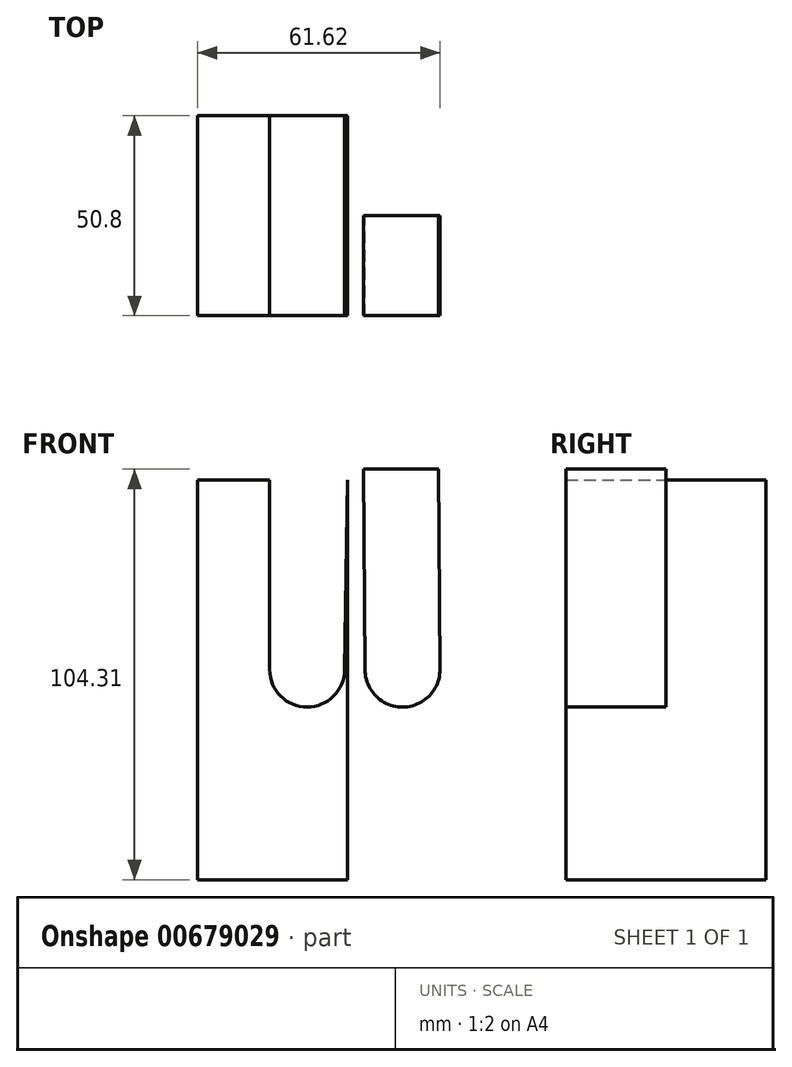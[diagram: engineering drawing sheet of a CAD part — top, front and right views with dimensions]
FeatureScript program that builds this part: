
annotation { "Feature Type Name" : "Feature", "Feature Type Description" : "" }
export const myFeature = defineFeature(function(context is Context, id is Id, definition is map)
    precondition{}
    {
        {
            var Q0;
            Q0=qCreatedBy(makeId("Front.planeOp"),FACE);
            var sketch = newSketch(context, id + "F0", { "sketchPlane" : qUnion([Q0])});
            skCircle(sketch, "E0", {"center": v(0, 0) * mm, "radius": 9.53 * mm});
            skLineSegment(sketch, "E1", {"start": v(-9.91, 50.92) * mm, "end": v(9.14, 50.92) * mm});
            skLineSegment(sketch, "E2", {"start": v(-9.52, 0) * mm, "end": v(-9.91, 50.92) * mm});
            skLineSegment(sketch, "E3", {"start": v(9.53, 0) * mm, "end": v(9.14, 50.92) * mm});
            skSolve(sketch);
        }
        {
            var Q0;
            Q0 = qSketchRegion(id + "F0", true);
            extrude(context, id + "F1", {"entities" : qUnion([Q0]), "depth" : 25.4 * mm, "offsetDistance" : 25.4 * mm});
        }
        {
            var Q0;
            Q0=qCreatedBy(makeId("Front.planeOp"),FACE);
            var sketch = newSketch(context, id + "F2", { "sketchPlane" : qUnion([Q0])});
            skLineSegment(sketch, "E4.bottom", {"start": v(-52.09, 48.2) * mm, "end": v(-13.99, 48.2) * mm});
            skLineSegment(sketch, "E4.top", {"start": v(-52.09, -53.4) * mm, "end": v(-13.99, -53.4) * mm});
            skLineSegment(sketch, "E4.left", {"start": v(-52.09, 48.2) * mm, "end": v(-52.09, -53.4) * mm});
            skLineSegment(sketch, "E4.right", {"start": v(-13.99, 48.2) * mm, "end": v(-13.99, -53.4) * mm});
            skCircle(sketch, "E5", {"center": v(-24.24, 0) * mm, "radius": 9.53 * mm});
            skLineSegment(sketch, "E6", {"start": v(-33.76, 0) * mm, "end": v(-33.76, 48.2) * mm});
            skLineSegment(sketch, "E7", {"start": v(-33.76, 0) * mm, "end": v(-14.71, 0) * mm});
            skLineSegment(sketch, "E8", {"start": v(-14.71, 0) * mm, "end": v(-13.99, 48.2) * mm});
            skSolve(sketch);
        }
        {
            var Q0;
            {var subQ2=sQuery(id+"F2.wireOp",EDGE,"E6");Q0=makeQuery(id+"F2.imprint","IMPRINT",FACE,{"disambiguationData":[TD([[makeQuery(id+"F2.imprint","IMPRINT",EDGE,{"derivedFrom":subQ2}),-1.0]])]});}
            var Q1;
            {var subQ0=sQuery(id+"F2.wireOp",EDGE,"E7");Q1=makeQuery(id+"F2.imprint","IMPRINT",FACE,{"disambiguationData":[TD([[makeQuery(id+"F2.imprint","IMPRINT",EDGE,{"derivedFrom":subQ0}),1.0]])]});}
            var Q2;
            {var subQ0=sQuery(id+"F2.wireOp",EDGE,"E7");Q2=makeQuery(id+"F2.imprint","IMPRINT",FACE,{"disambiguationData":[TD([[makeQuery(id+"F2.imprint","IMPRINT",EDGE,{"derivedFrom":subQ0}),-1.0]])]});}
            extrude(context, id + "F3", {"entities" : qUnion([Q0, Q1, Q2]), "operationType" : NewBodyOperationType.REMOVE, "oppositeDirection" : true, "depth" : 25.4 * mm, "offsetDistance" : 25.4 * mm});
        }
        {
            var Q0;
            Q0=makeQuery(id+"F2.imprint","IMPRINT",FACE,{"disambiguationData":[TD([[makeQuery(id+"F2.imprint","IMPRINT",EDGE,{"derivedFrom":sQuery(id+"F2.wireOp",EDGE,"E4.top")}),1.0]])]});
            extrude(context, id + "F4", {"entities" : qUnion([Q0]), "endBound" : BoundingType.SYMMETRIC, "depth" : 50.8 * mm, "offsetDistance" : 25.4 * mm});
        }
    });
